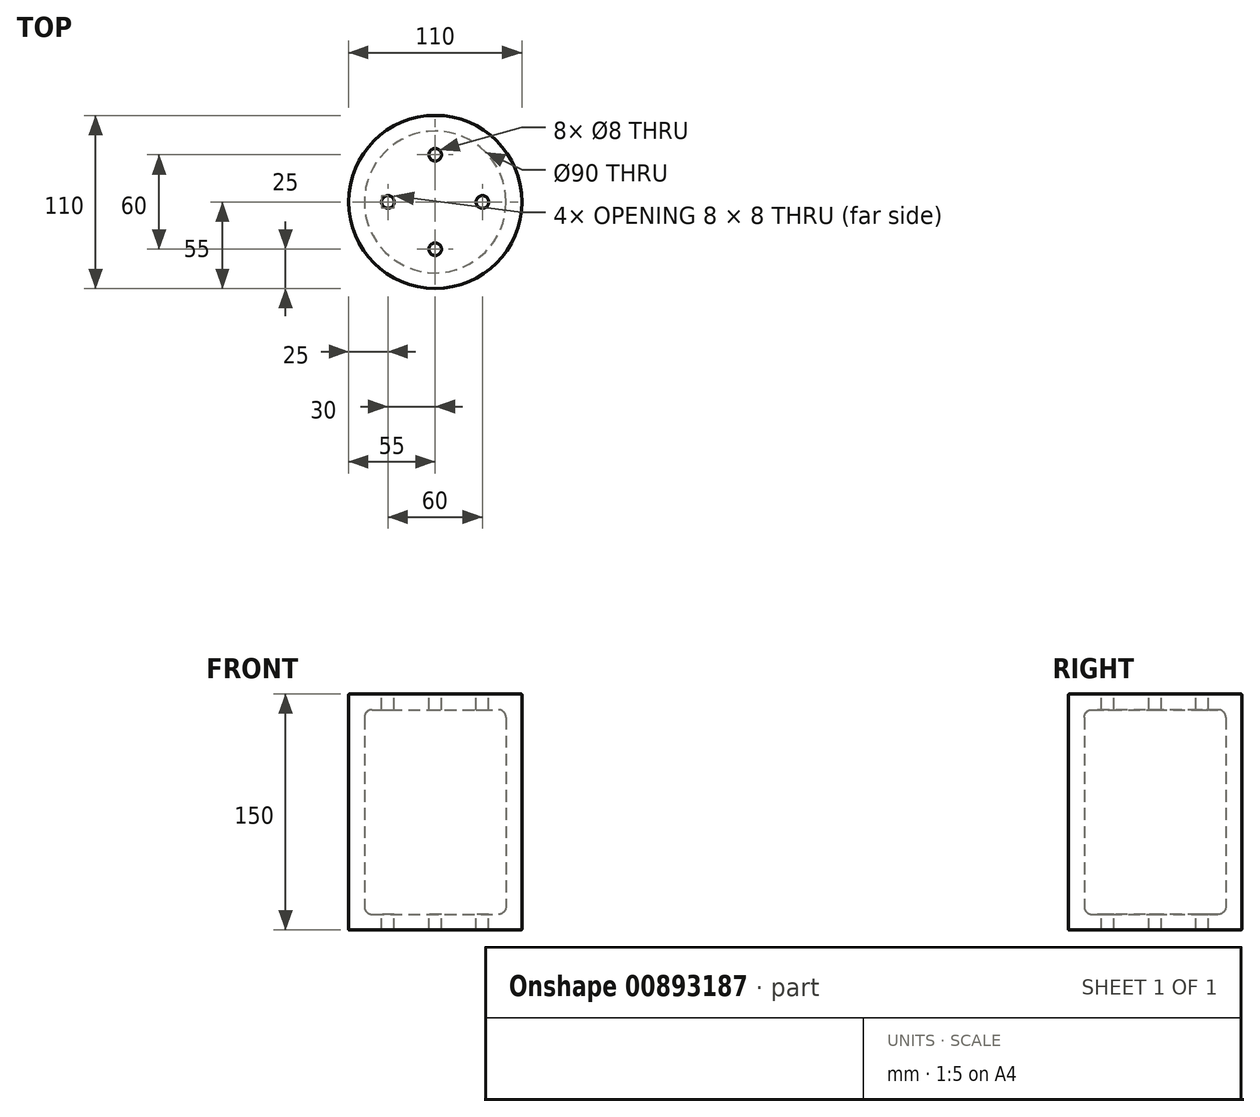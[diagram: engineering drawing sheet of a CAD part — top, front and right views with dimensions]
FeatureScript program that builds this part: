
annotation { "Feature Type Name" : "Feature", "Feature Type Description" : "" }
export const myFeature = defineFeature(function(context is Context, id is Id, definition is map)
    precondition{}
    {
        {
            var Q0;
            Q0=qCreatedBy(makeId("Front.planeOp"),FACE);
            var sketch = newSketch(context, id + "F0", { "sketchPlane" : qUnion([Q0])});
            skLineSegment(sketch, "E0", {"start": v(0, 0) * mm, "end": v(-54.5, 0) * mm});
            skLineSegment(sketch, "E1", {"start": v(-55, 0.5) * mm, "end": v(-55, 149.5) * mm});
            skLineSegment(sketch, "E2", {"start": v(-54.5, 150) * mm, "end": v(0, 150) * mm});
            skLineSegment(sketch, "E3", {"start": v(0, 150) * mm, "end": v(0, 140) * mm});
            skLineSegment(sketch, "E4", {"start": v(0, 140) * mm, "end": v(-40, 140) * mm});
            skLineSegment(sketch, "E5", {"start": v(-45, 135) * mm, "end": v(-45, 15) * mm});
            skLineSegment(sketch, "E6", {"start": v(-40, 10) * mm, "end": v(0, 10) * mm});
            skLineSegment(sketch, "E7", {"start": v(0, 10) * mm, "end": v(0, 0) * mm});
            skPoint(sketch, "E8.visualSharp", {"position": v(-45, 10) * mm});
            skArc(sketch, "E8.filletArc", {"start": v(-45, 15) * mm, "mid": v(-43.54, 11.46) * mm, "end": v(-40, 10) * mm});
            skPoint(sketch, "E9.visualSharp", {"position": v(-45, 140) * mm});
            skArc(sketch, "E9.filletArc", {"start": v(-40, 140) * mm, "mid": v(-43.54, 138.54) * mm, "end": v(-45, 135) * mm});
            skPoint(sketch, "E10.visualSharp", {"position": v(-55, 150) * mm});
            skArc(sketch, "E10.filletArc", {"start": v(-54.5, 150) * mm, "mid": v(-54.85, 149.85) * mm, "end": v(-55, 149.5) * mm});
            skPoint(sketch, "E11.visualSharp", {"position": v(-55, 0) * mm});
            skArc(sketch, "E11.filletArc", {"start": v(-55, 0.5) * mm, "mid": v(-54.85, 0.15) * mm, "end": v(-54.5, 0) * mm});
            skLineSegment(sketch, "E12", {"start": v(0, 35.25) * mm, "end": v(0, 61.3) * mm, "construction": true});
            skSolve(sketch);
        }
        {
            var Q0;
            Q0=makeQuery(id+"F0.imprint","IMPRINT",FACE,{"disambiguationData":[TD([[makeQuery(id+"F0.imprint","IMPRINT",EDGE,{"derivedFrom":sQuery(id+"F0.wireOp",EDGE,"E0")}),-1.0]])]});
            var Q1;
            Q1=sQuery(id+"F0.wireOp",EDGE,"E12");
            revolve(context, id + "F1", {"surfaceOperationType" : NewSurfaceOperationType.NEW, "entities" : qUnion([Q0]), "axis" : qUnion([Q1]), "revolveType" : RevolveType.FULL});
        }
        {
            var Q0;
            Q0=makeQuery(id+"F1.opRevolve","SWEPT_FACE",FACE,{"disambiguationData":[OSD([sQuery(id+"F0.wireOp",EDGE,"E2")])]});
            var sketch = newSketch(context, id + "F2", { "sketchPlane" : qUnion([Q0])});
            skCircle(sketch, "E13", {"center": v(0, 0) * mm, "radius": 30 * mm, "construction": true});
            skCircle(sketch, "E14", {"center": v(30, 0) * mm, "radius": 4 * mm});
            skCircle(sketch, "E15", {"center": v(0, -30) * mm, "radius": 4 * mm});
            skCircle(sketch, "E16", {"center": v(-30, 0) * mm, "radius": 4 * mm});
            skCircle(sketch, "E17", {"center": v(0, 30) * mm, "radius": 4 * mm});
            skSolve(sketch);
        }
        {
            var Q0;
            Q0=makeQuery(id+"F2.imprint","IMPRINT",FACE,{"disambiguationData":[TD([[makeQuery(id+"F2.imprint","IMPRINT",EDGE,{"derivedFrom":sQuery(id+"F2.wireOp",EDGE,"E14")}),1.0]])]});
            var Q1;
            Q1=makeQuery(id+"F2.imprint","IMPRINT",FACE,{"disambiguationData":[TD([[makeQuery(id+"F2.imprint","IMPRINT",EDGE,{"derivedFrom":sQuery(id+"F2.wireOp",EDGE,"E17")}),1.0]])]});
            var Q2;
            Q2=makeQuery(id+"F2.imprint","IMPRINT",FACE,{"disambiguationData":[TD([[makeQuery(id+"F2.imprint","IMPRINT",EDGE,{"derivedFrom":sQuery(id+"F2.wireOp",EDGE,"E16")}),1.0]])]});
            var Q3;
            Q3=makeQuery(id+"F2.imprint","IMPRINT",FACE,{"disambiguationData":[TD([[makeQuery(id+"F2.imprint","IMPRINT",EDGE,{"derivedFrom":sQuery(id+"F2.wireOp",EDGE,"E15")}),1.0]])]});
            extrude(context, id + "F3", {"entities" : qUnion([Q0, Q1, Q2, Q3]), "operationType" : NewBodyOperationType.REMOVE, "endBound" : BoundingType.THROUGH_ALL, "oppositeDirection" : true, "depth" : 25 * mm, "offsetDistance" : 25 * mm});
        }
    });
